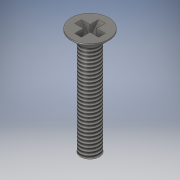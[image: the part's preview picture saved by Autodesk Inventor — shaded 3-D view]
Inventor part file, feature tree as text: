
AUTODESK INVENTOR PART (.ipt)
format: ipt  version: 2019 (Build 230136000, 136)  size: 137,728 bytes
history: native  units: mm
features: sketch x2, other x1, revolve x1, extrude x1, pattern_circular x1, thread x1
ambient origin geometry x8: Origin, YZ Plane, XZ Plane, XY Plane, X Axis, Y Axis, Z Axis, Center Point
bodies: Body1 (feature_tree)
feature tree (7):
  other  "Твердое тело1"
  revolve  "Вращение1"
  extrude  "Выдавливание1"  Depth=2.8mm
  pattern_circular  "Круговой массив1"  Angle=45.0deg  [1 undecoded]
  thread  "Резьба1"
  sketch  "Эскиз1"
  sketch  "Эскиз2"
note: 1 required parameter value undecoded (feature->parameter linkage not recoverable at this tier; creation-order binding heuristic only, values carry confidence <= 0.55)
